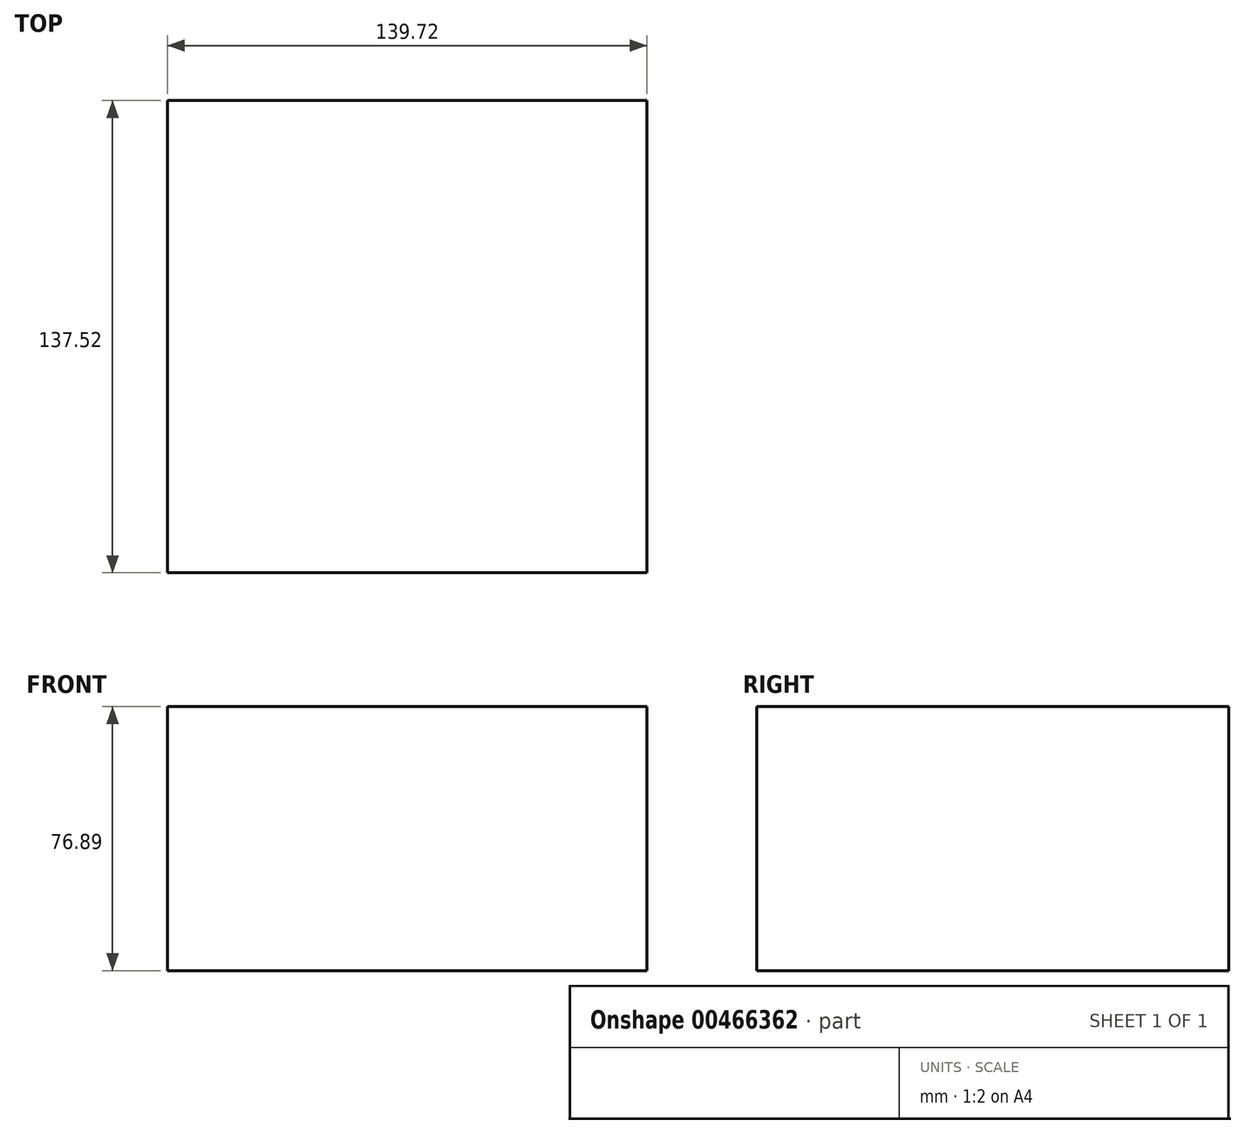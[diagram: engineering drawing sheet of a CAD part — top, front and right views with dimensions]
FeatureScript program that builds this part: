
annotation { "Feature Type Name" : "Feature", "Feature Type Description" : "" }
export const myFeature = defineFeature(function(context is Context, id is Id, definition is map)
    precondition{}
    {
        {
            var Q0;
            Q0=qCreatedBy(makeId("Top.planeOp"),FACE);
            var sketch = newSketch(context, id + "F0", { "sketchPlane" : qUnion([Q0])});
            skLineSegment(sketch, "E0.bottom", {"start": v(69.86, -68.76) * mm, "end": v(-69.86, -68.76) * mm});
            skLineSegment(sketch, "E0.top", {"start": v(69.86, 68.76) * mm, "end": v(-69.86, 68.76) * mm});
            skLineSegment(sketch, "E0.left", {"start": v(69.86, -68.76) * mm, "end": v(69.86, 68.76) * mm});
            skLineSegment(sketch, "E0.right", {"start": v(-69.86, -68.76) * mm, "end": v(-69.86, 68.76) * mm});
            skPoint(sketch, "E0.middle", {"position": v(0, 0) * mm});
            skLineSegment(sketch, "E1", {"start": v(0, 68.76) * mm, "end": v(0, -68.76) * mm});
            skSolve(sketch);
        }
        {
            var Q0;
            Q0=qCreatedBy(makeId("Top.planeOp"),FACE);
            var sketch = newSketch(context, id + "F1", { "sketchPlane" : qUnion([Q0])});
            skCircle(sketch, "E2", {"center": v(54.26, 0) * mm, "radius": 9.82 * mm});
            skSolve(sketch);
        }
        {
            var Q0;
            {var subQ0=sQuery(id+"F0.wireOp",EDGE,"E0.left");Q0=makeQuery(id+"F0.imprint","IMPRINT",FACE,{"disambiguationData":[TD([[makeQuery(id+"F0.imprint","IMPRINT",EDGE,{"derivedFrom":subQ0}),1.0]])]});}
            var Q1;
            {var subQ0=sQuery(id+"F0.wireOp",EDGE,"E0.right");Q1=makeQuery(id+"F0.imprint","IMPRINT",FACE,{"disambiguationData":[TD([[makeQuery(id+"F0.imprint","IMPRINT",EDGE,{"derivedFrom":subQ0}),-1.0]])]});}
            extrude(context, id + "F2", {"entities" : qUnion([Q0, Q1]), "oppositeDirection" : true, "depth" : 76.89 * mm});
        }
        {
            var Q0;
            Q0=sQuery(id+"F1.wireOp",EDGE,"E2");
            var Q1;
            Q1=sQuery(id+"F0.wireOp",EDGE,"E1");
            revolve(context, id + "F3", {"bodyType" : ToolBodyType.SURFACE, "surfaceEntities" : qUnion([Q0]), "axis" : qUnion([Q1]), "revolveType" : RevolveType.FULL});
        }
    });
